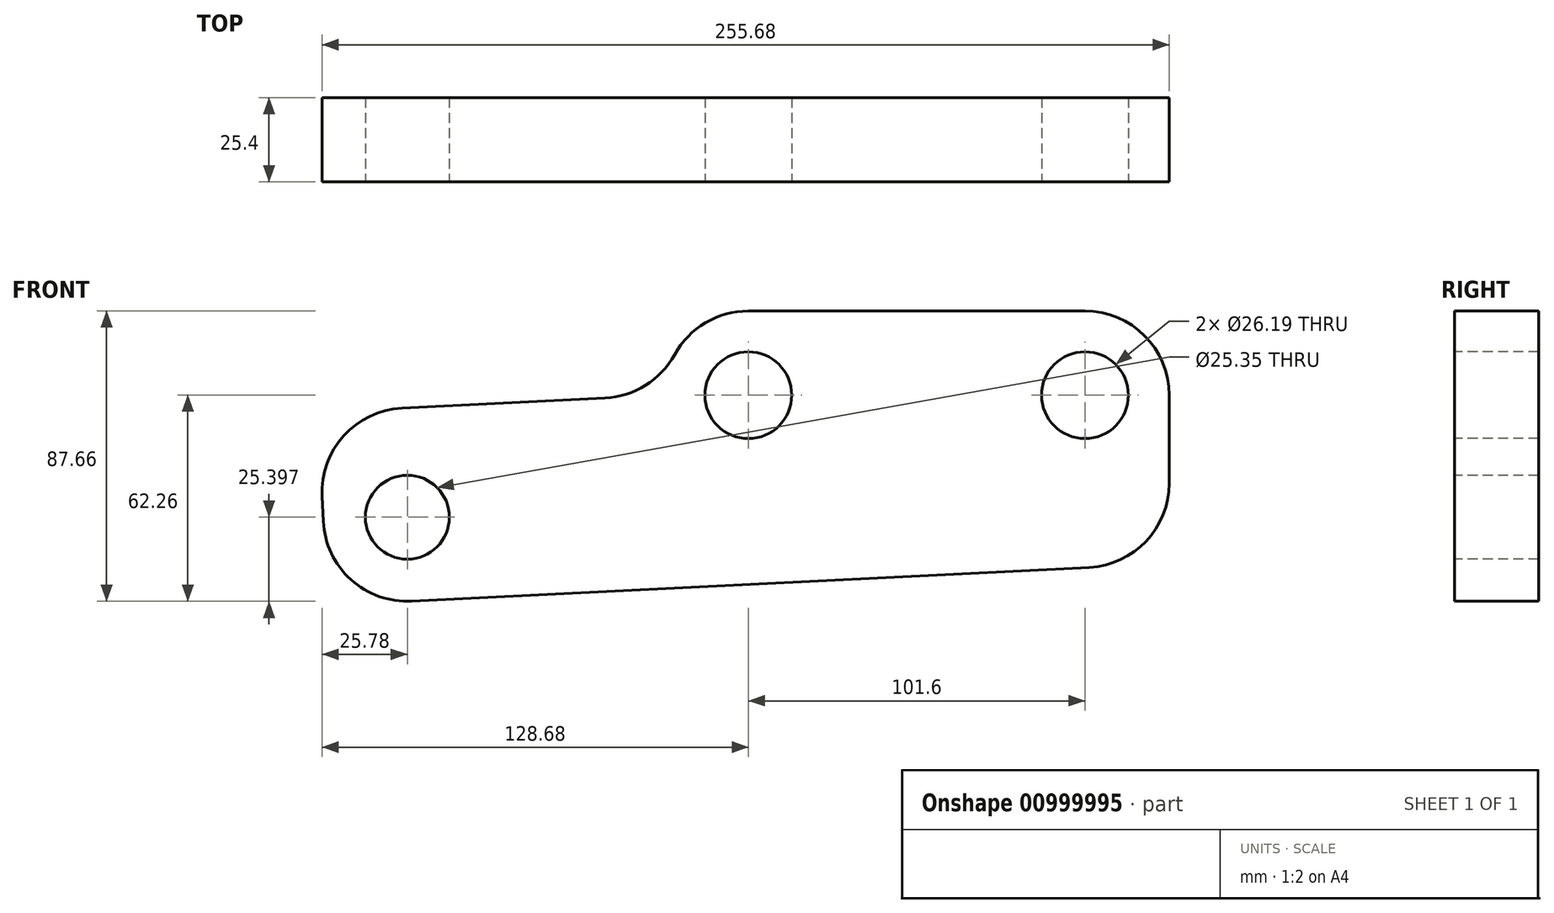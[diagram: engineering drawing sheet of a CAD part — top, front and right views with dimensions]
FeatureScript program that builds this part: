
annotation { "Feature Type Name" : "Feature", "Feature Type Description" : "" }
export const myFeature = defineFeature(function(context is Context, id is Id, definition is map)
    precondition{}
    {
        {
            var Q0;
            Q0=qCreatedBy(makeId("Front.planeOp"),FACE);
            var sketch = newSketch(context, id + "F0", { "sketchPlane" : qUnion([Q0])});
            skLineSegment(sketch, "E0.bottom", {"start": v(76.2, -12.7) * mm, "end": v(-76.2, -12.7) * mm});
            skLineSegment(sketch, "E0.top", {"start": v(76.2, 12.7) * mm, "end": v(-76.2, 12.7) * mm});
            skLineSegment(sketch, "E0.left", {"start": v(76.2, -12.7) * mm, "end": v(76.2, 12.7) * mm});
            skLineSegment(sketch, "E0.right", {"start": v(-76.2, -12.7) * mm, "end": v(-76.2, 12.7) * mm});
            skPoint(sketch, "E0.middle", {"position": v(0, 0) * mm});
            skCircle(sketch, "E1", {"center": v(-50.8, 38.1) * mm, "radius": 25.4 * mm});
            skCircle(sketch, "E2", {"center": v(50.8, 38.1) * mm, "radius": 25.4 * mm});
            skLineSegment(sketch, "E3", {"start": v(-76.2, 12.7) * mm, "end": v(-76.2, 38.1) * mm});
            skLineSegment(sketch, "E4", {"start": v(76.2, 38.1) * mm, "end": v(76.2, 12.7) * mm});
            skLineSegment(sketch, "E5", {"start": v(76.2, -12.7) * mm, "end": v(-177.8, -25.4) * mm});
            skLineSegment(sketch, "E6", {"start": v(-177.8, -25.4) * mm, "end": v(-180.71, 32.87) * mm});
            skLineSegment(sketch, "E7", {"start": v(-50.8, 63.5) * mm, "end": v(50.8, 63.5) * mm});
            skLineSegment(sketch, "E8", {"start": v(-76.2, 38.1) * mm, "end": v(-180.71, 32.87) * mm});
            skSolve(sketch);
        }
        {
            var Q0;
            {var subQ0=sQuery(id+"F0.wireOp",EDGE,"E1");var subQ1=makeQuery(id+"F0.imprint","INTERSECT",VERTEX,{"derivedFrom":[subQ0,sQuery(id+"F0.wireOp",EDGE,"E3")]});Q0=makeQuery(id+"F0.imprint","IMPRINT",FACE,{"disambiguationData":[TD([[makeQuery(id+"F0.imprint","IMPRINT",EDGE,{"disambiguationData":[TD([[subQ1,1.0]])],"derivedFrom":subQ0}),1.0]])]});}
            var Q1;
            {var subQ0=sQuery(id+"F0.wireOp",EDGE,"E3");Q1=makeQuery(id+"F0.imprint","IMPRINT",FACE,{"disambiguationData":[TD([[makeQuery(id+"F0.imprint","IMPRINT",EDGE,{"derivedFrom":subQ0}),-1.0]])]});}
            var Q2;
            Q2=makeQuery(id+"F0.imprint","IMPRINT",FACE,{"disambiguationData":[TD([[makeQuery(id+"F0.imprint","IMPRINT",EDGE,{"derivedFrom":sQuery(id+"F0.wireOp",EDGE,"E0.bottom")}),-1.0]])]});
            var Q3;
            {var subQ0=sQuery(id+"F0.wireOp",EDGE,"RRI4nu7H-9loL-EgaG-OxSV-4ZIok2e90qct");Q3=makeQuery(id+"F0.imprint","IMPRINT",FACE,{"disambiguationData":[TD([[makeQuery(id+"F0.imprint","IMPRINT",EDGE,{"derivedFrom":subQ0}),-1.0]])]});}
            var Q4;
            {var subQ0=sQuery(id+"F0.wireOp",EDGE,"OTc06pxV-o9xx-F76t-7mBi-RcyUqe5OUzu3");Q4=makeQuery(id+"F0.imprint","IMPRINT",FACE,{"disambiguationData":[TD([[makeQuery(id+"F0.imprint","IMPRINT",EDGE,{"derivedFrom":subQ0}),1.0]])]});}
            var Q5;
            {var subQ0=sQuery(id+"F0.wireOp",EDGE,"E4");Q5=makeQuery(id+"F0.imprint","IMPRINT",FACE,{"disambiguationData":[TD([[makeQuery(id+"F0.imprint","IMPRINT",EDGE,{"derivedFrom":subQ0}),-1.0]])]});}
            var Q6;
            {var subQ0=sQuery(id+"F0.wireOp",EDGE,"E2");var subQ1=makeQuery(id+"F0.imprint","INTERSECT",VERTEX,{"derivedFrom":[subQ0,sQuery(id+"F0.wireOp",EDGE,"OTc06pxV-o9xx-F76t-7mBi-RcyUqe5OUzu3")]});Q6=makeQuery(id+"F0.imprint","IMPRINT",FACE,{"disambiguationData":[TD([[makeQuery(id+"F0.imprint","IMPRINT",EDGE,{"disambiguationData":[TD([[subQ1,-1.0]])],"derivedFrom":subQ0}),1.0]])]});}
            var Q7;
            Q7=makeQuery(id+"F0.imprint","IMPRINT",FACE,{"disambiguationData":[TD([[makeQuery(id+"F0.imprint","IMPRINT",EDGE,{"derivedFrom":sQuery(id+"F0.wireOp",EDGE,"E0.bottom")}),1.0]])]});
            var Q8;
            {var subQ5=sQuery(id+"F0.wireOp",EDGE,"E7");Q8=makeQuery(id+"F0.imprint","IMPRINT",FACE,{"disambiguationData":[TD([[makeQuery(id+"F0.imprint","IMPRINT",EDGE,{"derivedFrom":subQ5}),-1.0]])]});}
            extrude(context, id + "F1", {"entities" : qUnion([Q0, Q1, Q2, Q3, Q4, Q5, Q6, Q7, Q8]), "depth" : 25.4 * mm, "offsetDistance" : 25.4 * mm});
        }
        {
            var Q0;
            Q0=makeQuery(id+"F1.opExtrude","CAP_FACE",FACE,{"disambiguationData":[OSD([sQuery(id+"F0.wireOp",EDGE,"E0.bottom"),sQuery(id+"F0.wireOp",EDGE,"E0.top"),sQuery(id+"F0.wireOp",EDGE,"E0.left"),sQuery(id+"F0.wireOp",EDGE,"E0.right"),sQuery(id+"F0.wireOp",EDGE,"E1"),sQuery(id+"F0.wireOp",EDGE,"E2"),sQuery(id+"F0.wireOp",EDGE,"E3"),sQuery(id+"F0.wireOp",EDGE,"RRI4nu7H-9loL-EgaG-OxSV-4ZIok2e90qct"),sQuery(id+"F0.wireOp",EDGE,"OTc06pxV-o9xx-F76t-7mBi-RcyUqe5OUzu3"),sQuery(id+"F0.wireOp",EDGE,"E4")])],"isStart":false});
            var sketch = newSketch(context, id + "F2", { "sketchPlane" : qUnion([Q0])});
            skPoint(sketch, "E9", {"position": v(-50.8, 38.1) * mm});
            skPoint(sketch, "E10", {"position": v(50.8, 38.1) * mm});
            skSolve(sketch);
        }
        {
            var Q0;
            Q0=sQuery(id+"F2.wireOp",VERTEX,"E9");
            var Q1;
            Q1=sQuery(id+"F2.wireOp",VERTEX,"E10");
            var Q2;
            Q2=makeQuery(id+"F1.opExtrude","SWEPT_BODY",BODY,{"disambiguationData":[OSD([sQuery(id+"F0.wireOp",EDGE,"E0.bottom"),sQuery(id+"F0.wireOp",EDGE,"E0.top"),sQuery(id+"F0.wireOp",EDGE,"E0.left"),sQuery(id+"F0.wireOp",EDGE,"E0.right"),sQuery(id+"F0.wireOp",EDGE,"E1"),sQuery(id+"F0.wireOp",EDGE,"E2"),sQuery(id+"F0.wireOp",EDGE,"E3"),sQuery(id+"F0.wireOp",EDGE,"RRI4nu7H-9loL-EgaG-OxSV-4ZIok2e90qct"),sQuery(id+"F0.wireOp",EDGE,"OTc06pxV-o9xx-F76t-7mBi-RcyUqe5OUzu3"),sQuery(id+"F0.wireOp",EDGE,"E4")])]});
            hole(context, id + "F3", {"style" : HoleStyle.SIMPLE, "endStyle" : HoleEndStyle.THROUGH, "standardTappedOrClearance" : lookupTablePath({ "fit" : "Close (ASME)", "standard" : "ANSI", "size" : "1", "type" : "Clearance" }), "standardBlindInLast" : lookupTablePath({ "fit" : "Close", "standard" : "ANSI", "engagement" : "75%", "pitch" : "8 tpi", "size" : "1", "type" : "Clearance & tapped" }), "holeDiameter" : 26.2 * mm, "majorDiameter" : 6.35 * mm, "isTappedThrough" : true, "tappedDepth" : 12.7 * mm, "tapClearance" : 3, "locations" : qUnion([Q0, Q1]), "scope" : qUnion([Q2])});
        }
        {
            var Q0;
            Q0=makeQuery(id+"F1.opExtrude","SWEPT_EDGE",EDGE,{"disambiguationData":[OSD([sQuery(id+"F0.wireOp",EDGE,"E0.bottom"),sQuery(id+"F0.wireOp",EDGE,"E0.left"),sQuery(id+"F0.wireOp",EDGE,"E5")])]});
            var Q1;
            Q1=makeQuery(id+"F1.opExtrude","SWEPT_EDGE",EDGE,{"disambiguationData":[OSD([sQuery(id+"F0.wireOp",EDGE,"E6"),sQuery(id+"F0.wireOp",EDGE,"a9V4RTfo-RdVa-lRmL-kq9R-w78Rz7kxsgNC")])]});
            var Q2;
            Q2=makeQuery(id+"F1.opExtrude","SWEPT_EDGE",EDGE,{"disambiguationData":[OSD([sQuery(id+"F0.wireOp",EDGE,"E5"),sQuery(id+"F0.wireOp",EDGE,"E6")])]});
            var Q3;
            Q3=makeQuery(id+"F1.opExtrude","SWEPT_EDGE",EDGE,{"disambiguationData":[OSD([sQuery(id+"F0.wireOp",EDGE,"E0.right"),sQuery(id+"F0.wireOp",EDGE,"a9V4RTfo-RdVa-lRmL-kq9R-w78Rz7kxsgNC")])]});
            var Q4;
            Q4=makeQuery(id+"F1.opExtrude","SWEPT_EDGE",EDGE,{"disambiguationData":[OSD([sQuery(id+"F0.wireOp",EDGE,"E1"),sQuery(id+"F0.wireOp",EDGE,"E3"),sQuery(id+"F0.wireOp",EDGE,"E8")])]});
            fillet(context, id + "F4", {"entities" : qUnion([Q0, Q1, Q2, Q3, Q4]), "radius" : 25.4 * mm, "tangentPropagation" : true, "allowEdgeOverflow" : false});
        }
        {
            var Q0;
            Q0=makeQuery(id+"F1.opExtrude","CAP_FACE",FACE,{"disambiguationData":[OSD([sQuery(id+"F0.wireOp",EDGE,"E0.top"),sQuery(id+"F0.wireOp",EDGE,"E0.left"),sQuery(id+"F0.wireOp",EDGE,"E0.right"),sQuery(id+"F0.wireOp",EDGE,"E1"),sQuery(id+"F0.wireOp",EDGE,"E2"),sQuery(id+"F0.wireOp",EDGE,"E3"),sQuery(id+"F0.wireOp",EDGE,"RRI4nu7H-9loL-EgaG-OxSV-4ZIok2e90qct"),sQuery(id+"F0.wireOp",EDGE,"OTc06pxV-o9xx-F76t-7mBi-RcyUqe5OUzu3"),sQuery(id+"F0.wireOp",EDGE,"E4"),sQuery(id+"F0.wireOp",EDGE,"E5"),sQuery(id+"F0.wireOp",EDGE,"E6"),sQuery(id+"F0.wireOp",EDGE,"a9V4RTfo-RdVa-lRmL-kq9R-w78Rz7kxsgNC")])],"isStart":false});
            var sketch = newSketch(context, id + "F5", { "sketchPlane" : qUnion([Q0])});
            skPoint(sketch, "E11", {"position": v(-51.64, 10.12) * mm});
            skLineSegment(sketch, "E12", {"start": v(-50.18, -19.02) * mm, "end": v(-53.1, 39.26) * mm, "construction": true});
            skSolve(sketch);
        }
        {
            var Q0;
            {var subQ8=sQuery(id+"F0.wireOp",EDGE,"E1");Q0=makeQuery(id+"F5.imprint","IMPRINT",FACE,{"disambiguationData":[TD([[makeQuery(id+"F5.imprint","IMPRINT",EDGE,{"derivedFrom":makeQuery(id+"F1.opExtrude","CAP_EDGE",EDGE,{"disambiguationData":[OSD([subQ8])],"isStart":false})}),1.0]])]});}
            var sketch = newSketch(context, id + "F6", { "sketchPlane" : qUnion([Q0])});
            skPoint(sketch, "E13", {"position": v(-153.7, 1.24) * mm});
            skSolve(sketch);
        }
        {
            var Q0;
            Q0=sQuery(id+"F6.wireOp",VERTEX,"E13");
            var Q1;
            Q1=makeQuery(id+"F1.opExtrude","SWEPT_BODY",BODY,{"disambiguationData":[OSD([sQuery(id+"F0.wireOp",EDGE,"E0.top"),sQuery(id+"F0.wireOp",EDGE,"E0.left"),sQuery(id+"F0.wireOp",EDGE,"E0.right"),sQuery(id+"F0.wireOp",EDGE,"E1"),sQuery(id+"F0.wireOp",EDGE,"E2"),sQuery(id+"F0.wireOp",EDGE,"E3"),sQuery(id+"F0.wireOp",EDGE,"RRI4nu7H-9loL-EgaG-OxSV-4ZIok2e90qct"),sQuery(id+"F0.wireOp",EDGE,"OTc06pxV-o9xx-F76t-7mBi-RcyUqe5OUzu3"),sQuery(id+"F0.wireOp",EDGE,"E4"),sQuery(id+"F0.wireOp",EDGE,"E5"),sQuery(id+"F0.wireOp",EDGE,"E6"),sQuery(id+"F0.wireOp",EDGE,"a9V4RTfo-RdVa-lRmL-kq9R-w78Rz7kxsgNC")])]});
            hole(context, id + "F7", {"style" : HoleStyle.SIMPLE, "endStyle" : HoleEndStyle.THROUGH, "holeDiameter" : 25.35 * mm, "majorDiameter" : 6.35 * mm, "isTappedThrough" : true, "tappedDepth" : 12.7 * mm, "tapClearance" : 3, "locations" : qUnion([Q0]), "scope" : qUnion([Q1])});
        }
    });
